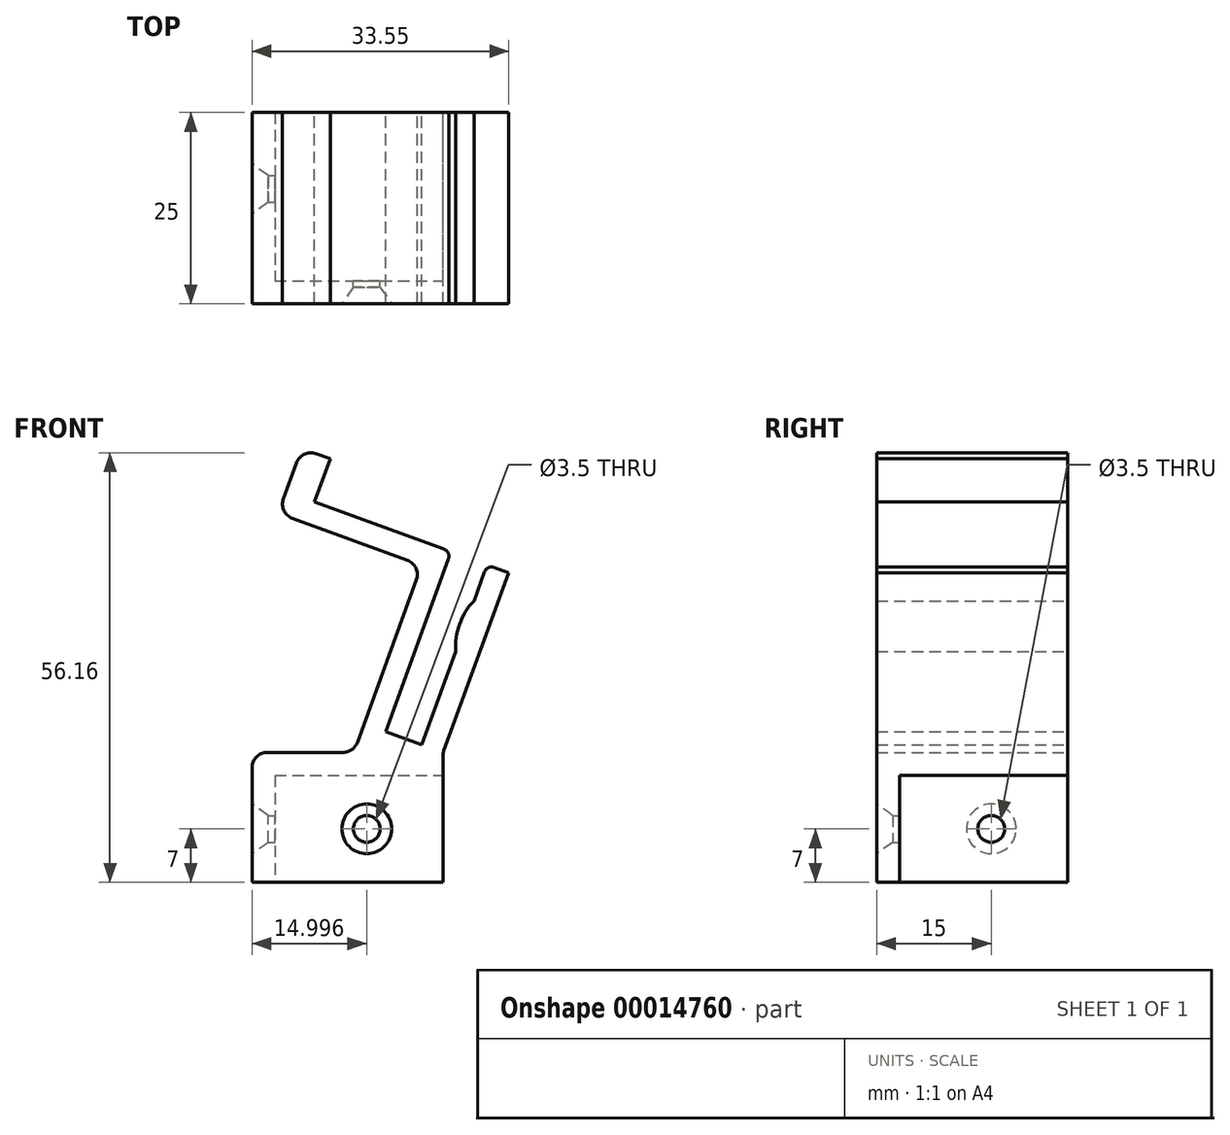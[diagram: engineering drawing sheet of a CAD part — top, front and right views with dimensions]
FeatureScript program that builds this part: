
annotation { "Feature Type Name" : "Feature", "Feature Type Description" : "" }
export const myFeature = defineFeature(function(context is Context, id is Id, definition is map)
    precondition{}
    {
        {
            var Q0;
            Q0=qCreatedBy(makeId("Front.planeOp"),FACE);
            var sketch = newSketch(context, id + "F0", { "sketchPlane" : qUnion([Q0])});
            skLineSegment(sketch, "E0", {"start": v(-18.57, 0) * mm, "end": v(-18.57, 1) * mm});
            skLineSegment(sketch, "E1", {"start": v(-10.2, 42.04) * mm, "end": v(-8.34, 41.37) * mm});
            skLineSegment(sketch, "E2", {"start": v(-8.34, 41.37) * mm, "end": v(-10.4, 35.73) * mm});
            skLineSegment(sketch, "E3", {"start": v(-10.4, 35.73) * mm, "end": v(6.52, 29.57) * mm});
            skLineSegment(sketch, "E4", {"start": v(7.12, 28.29) * mm, "end": v(-1.1, 5.74) * mm});
            skLineSegment(sketch, "E5", {"start": v(-1.1, 5.74) * mm, "end": v(3.6, 4.03) * mm});
            skLineSegment(sketch, "E6", {"start": v(3.6, 4.03) * mm, "end": v(8.04, 16.2) * mm});
            skArc(sketch, "E7", {"start": v(10.45, 22.82) * mm, "mid": v(8.56, 19.76) * mm, "end": v(8.04, 16.2) * mm});
            skLineSegment(sketch, "E8", {"start": v(10.45, 22.82) * mm, "end": v(11.82, 26.58) * mm});
            skLineSegment(sketch, "E9", {"start": v(13.1, 27.18) * mm, "end": v(14.98, 26.5) * mm});
            skLineSegment(sketch, "E10", {"start": v(14.98, 26.5) * mm, "end": v(6.49, 3.17) * mm});
            skLineSegment(sketch, "E11", {"start": v(6.43, 2.82) * mm, "end": v(6.43, 0) * mm});
            skLineSegment(sketch, "E12", {"start": v(6.43, 0) * mm, "end": v(-18.57, 0) * mm});
            skLineSegment(sketch, "E13", {"start": v(7.46, 29.23) * mm, "end": v(11.02, 27.93) * mm, "construction": true});
            skLineSegment(sketch, "E14", {"start": v(3.6, 4.03) * mm, "end": v(9.61, 1.84) * mm, "construction": true});
            skLineSegment(sketch, "E15", {"start": v(-12.76, 40.85) * mm, "end": v(-14.47, 36.15) * mm});
            skPoint(sketch, "E15.endSnap0", {"position": v(-18.57, 19.9) * mm});
            skPoint(sketch, "E16.orphan", {"position": v(-18.57, 39.81) * mm});
            skLineSegment(sketch, "E17", {"start": v(-18.57, 0) * mm, "end": v(-18.57, -14) * mm});
            skLineSegment(sketch, "E18", {"start": v(-18.57, -14) * mm, "end": v(6.43, -14) * mm});
            skLineSegment(sketch, "E19", {"start": v(6.43, -14) * mm, "end": v(6.43, 0) * mm});
            skPoint(sketch, "E20.visualSharp", {"position": v(-18.57, 24.88) * mm});
            skPoint(sketch, "E21.visualSharp", {"position": v(-12.08, 42.73) * mm});
            skArc(sketch, "E21.filletArc", {"start": v(-10.2, 42.04) * mm, "mid": v(-11.73, 41.97) * mm, "end": v(-12.76, 40.85) * mm});
            skPoint(sketch, "E22.visualSharp", {"position": v(12.16, 27.52) * mm});
            skArc(sketch, "E22.filletArc", {"start": v(13.1, 27.18) * mm, "mid": v(12.33, 27.14) * mm, "end": v(11.82, 26.58) * mm});
            skPoint(sketch, "E23.visualSharp", {"position": v(7.46, 29.23) * mm});
            skArc(sketch, "E23.filletArc", {"start": v(7.12, 28.29) * mm, "mid": v(7.08, 29.05) * mm, "end": v(6.52, 29.57) * mm});
            skPoint(sketch, "E24.visualSharp", {"position": v(6.43, 3) * mm});
            skArc(sketch, "E24.filletArc", {"start": v(6.49, 3.17) * mm, "mid": v(6.44, 3) * mm, "end": v(6.43, 2.82) * mm});
            skLineSegment(sketch, "E25", {"start": v(-9.68, 32.27) * mm, "end": v(1.73, 28.12) * mm});
            skLineSegment(sketch, "E26", {"start": v(2.93, 25.56) * mm, "end": v(-4.8, 4.32) * mm});
            skLineSegment(sketch, "E27", {"start": v(-9.68, 32.27) * mm, "end": v(-13.28, 33.58) * mm});
            skLineSegment(sketch, "E28", {"start": v(-6.68, 3) * mm, "end": v(-16.57, 3) * mm});
            skPoint(sketch, "E29.orphan", {"position": v(-4.8, 3) * mm});
            skPoint(sketch, "E30.visualSharp", {"position": v(-15.16, 34.27) * mm});
            skArc(sketch, "E30.filletArc", {"start": v(-14.47, 36.15) * mm, "mid": v(-14.4, 34.62) * mm, "end": v(-13.28, 33.58) * mm});
            skPoint(sketch, "E31.visualSharp", {"position": v(-18.57, 3) * mm});
            skArc(sketch, "E31.filletArc", {"start": v(-16.57, 3) * mm, "mid": v(-17.99, 2.41) * mm, "end": v(-18.57, 1) * mm});
            skPoint(sketch, "E32.visualSharp", {"position": v(3.61, 27.44) * mm});
            skArc(sketch, "E32.filletArc", {"start": v(2.93, 25.56) * mm, "mid": v(2.86, 27.09) * mm, "end": v(1.73, 28.12) * mm});
            skPoint(sketch, "E33.visualSharp", {"position": v(-5.28, 3) * mm});
            skArc(sketch, "E33.filletArc", {"start": v(-6.68, 3) * mm, "mid": v(-5.53, 3.36) * mm, "end": v(-4.8, 4.32) * mm});
            skSolve(sketch);
        }
        {
            var Q0;
            Q0=makeQuery(id+"F0.imprint","IMPRINT",FACE,{"disambiguationData":[TD([[makeQuery(id+"F0.imprint","IMPRINT",EDGE,{"derivedFrom":sQuery(id+"F0.wireOp",EDGE,"E0")}),-1.0]])]});
            var Q1;
            Q1=makeQuery(id+"F0.imprint","IMPRINT",FACE,{"disambiguationData":[TD([[makeQuery(id+"F0.imprint","IMPRINT",EDGE,{"derivedFrom":sQuery(id+"F0.wireOp",EDGE,"E12")}),1.0]])]});
            extrude(context, id + "F1", {"entities" : qUnion([Q0, Q1]), "depth" : 25 * mm});
        }
        {
            var Q0;
            Q0=makeQuery(id+"F1.opExtrude","SWEPT_FACE",FACE,{"disambiguationData":[OSD([sQuery(id+"F0.wireOp",EDGE,"E18")])]});
            var sketch = newSketch(context, id + "F2", { "sketchPlane" : qUnion([Q0])});
            skLineSegment(sketch, "E34.bottom", {"start": v(-15.57, 0) * mm, "end": v(6.43, 0) * mm});
            skLineSegment(sketch, "E34.top", {"start": v(-15.57, 22) * mm, "end": v(6.43, 22) * mm});
            skLineSegment(sketch, "E34.left", {"start": v(-15.57, 0) * mm, "end": v(-15.57, 22) * mm});
            skLineSegment(sketch, "E34.right", {"start": v(6.43, 0) * mm, "end": v(6.43, 22) * mm});
            skSolve(sketch);
        }
        {
            var Q0;
            Q0=makeQuery(id+"F2.imprint","IMPRINT",FACE,{"disambiguationData":[TD([[makeQuery(id+"F2.imprint","IMPRINT",EDGE,{"derivedFrom":sQuery(id+"F2.wireOp",EDGE,"E34.bottom")}),1.0]])]});
            extrude(context, id + "F3", {"entities" : qUnion([Q0]), "operationType" : NewBodyOperationType.REMOVE, "oppositeDirection" : true, "depth" : 14 * mm});
        }
        {
            var Q0;
            Q0=makeQuery(id+"F1.opExtrude","CAP_FACE",FACE,{"disambiguationData":[OSD([sQuery(id+"F0.wireOp",EDGE,"E0"),sQuery(id+"F0.wireOp",EDGE,"E1"),sQuery(id+"F0.wireOp",EDGE,"E2"),sQuery(id+"F0.wireOp",EDGE,"E3"),sQuery(id+"F0.wireOp",EDGE,"E4"),sQuery(id+"F0.wireOp",EDGE,"E5"),sQuery(id+"F0.wireOp",EDGE,"E6"),sQuery(id+"F0.wireOp",EDGE,"E7"),sQuery(id+"F0.wireOp",EDGE,"E8"),sQuery(id+"F0.wireOp",EDGE,"E9"),sQuery(id+"F0.wireOp",EDGE,"E10"),sQuery(id+"F0.wireOp",EDGE,"E11"),sQuery(id+"F0.wireOp",EDGE,"E15"),sQuery(id+"F0.wireOp",EDGE,"E17"),sQuery(id+"F0.wireOp",EDGE,"E18"),sQuery(id+"F0.wireOp",EDGE,"E19"),sQuery(id+"F0.wireOp",EDGE,"E20.filletArc"),sQuery(id+"F0.wireOp",EDGE,"E21.filletArc"),sQuery(id+"F0.wireOp",EDGE,"E22.filletArc"),sQuery(id+"F0.wireOp",EDGE,"E23.filletArc"),sQuery(id+"F0.wireOp",EDGE,"E24.filletArc")])],"isStart":false});
            var sketch = newSketch(context, id + "F4", { "sketchPlane" : qUnion([Q0])});
            skPoint(sketch, "E35", {"position": v(-3.57, -7) * mm});
            skSolve(sketch);
        }
        {
            var Q0;
            Q0=makeQuery(id+"F1.opExtrude","SWEPT_FACE",FACE,{"disambiguationData":[OSD([sQuery(id+"F0.wireOp",EDGE,"E0"),sQuery(id+"F0.wireOp",EDGE,"E17")])]});
            var sketch = newSketch(context, id + "F5", { "sketchPlane" : qUnion([Q0])});
            skPoint(sketch, "E36", {"position": v(10, -7) * mm});
            skSolve(sketch);
        }
        {
            var Q0;
            Q0=sQuery(id+"F5.wireOp",VERTEX,"E36");
            var Q1;
            Q1=makeQuery(id+"F1.opExtrude","SWEPT_BODY",BODY,{"disambiguationData":[OSD([sQuery(id+"F0.wireOp",EDGE,"E0"),sQuery(id+"F0.wireOp",EDGE,"E1"),sQuery(id+"F0.wireOp",EDGE,"E2"),sQuery(id+"F0.wireOp",EDGE,"E3"),sQuery(id+"F0.wireOp",EDGE,"E4"),sQuery(id+"F0.wireOp",EDGE,"E5"),sQuery(id+"F0.wireOp",EDGE,"E6"),sQuery(id+"F0.wireOp",EDGE,"E7"),sQuery(id+"F0.wireOp",EDGE,"E8"),sQuery(id+"F0.wireOp",EDGE,"E9"),sQuery(id+"F0.wireOp",EDGE,"E10"),sQuery(id+"F0.wireOp",EDGE,"E11"),sQuery(id+"F0.wireOp",EDGE,"E15"),sQuery(id+"F0.wireOp",EDGE,"E17"),sQuery(id+"F0.wireOp",EDGE,"E18"),sQuery(id+"F0.wireOp",EDGE,"E19"),sQuery(id+"F0.wireOp",EDGE,"E20.filletArc"),sQuery(id+"F0.wireOp",EDGE,"E21.filletArc"),sQuery(id+"F0.wireOp",EDGE,"E22.filletArc"),sQuery(id+"F0.wireOp",EDGE,"E23.filletArc"),sQuery(id+"F0.wireOp",EDGE,"E24.filletArc")])]});
            hole(context, id + "F6", {"style" : HoleStyle.C_SINK, "endStyle" : HoleEndStyle.BLIND, "holeDiameter" : 3.5 * mm, "cSinkDiameter" : 6.5 * mm, "cSinkAngle" : 70 * degree, "holeDepth" : 6 * mm, "locations" : qUnion([Q0]), "scope" : qUnion([Q1]), "startStyle" : HoleStartStyle.SKETCH});
        }
        {
            var Q0;
            Q0=sQuery(id+"F4.wireOp",VERTEX,"E35");
            var Q1;
            Q1=makeQuery(id+"F1.opExtrude","SWEPT_BODY",BODY,{"disambiguationData":[OSD([sQuery(id+"F0.wireOp",EDGE,"E0"),sQuery(id+"F0.wireOp",EDGE,"E1"),sQuery(id+"F0.wireOp",EDGE,"E2"),sQuery(id+"F0.wireOp",EDGE,"E3"),sQuery(id+"F0.wireOp",EDGE,"E4"),sQuery(id+"F0.wireOp",EDGE,"E5"),sQuery(id+"F0.wireOp",EDGE,"E6"),sQuery(id+"F0.wireOp",EDGE,"E7"),sQuery(id+"F0.wireOp",EDGE,"E8"),sQuery(id+"F0.wireOp",EDGE,"E9"),sQuery(id+"F0.wireOp",EDGE,"E10"),sQuery(id+"F0.wireOp",EDGE,"E11"),sQuery(id+"F0.wireOp",EDGE,"E15"),sQuery(id+"F0.wireOp",EDGE,"E17"),sQuery(id+"F0.wireOp",EDGE,"E18"),sQuery(id+"F0.wireOp",EDGE,"E19"),sQuery(id+"F0.wireOp",EDGE,"E20.filletArc"),sQuery(id+"F0.wireOp",EDGE,"E21.filletArc"),sQuery(id+"F0.wireOp",EDGE,"E22.filletArc"),sQuery(id+"F0.wireOp",EDGE,"E23.filletArc"),sQuery(id+"F0.wireOp",EDGE,"E24.filletArc")])]});
            hole(context, id + "F7", {"style" : HoleStyle.C_SINK, "endStyle" : HoleEndStyle.BLIND, "holeDiameter" : 3.5 * mm, "cSinkDiameter" : 6.5 * mm, "cSinkAngle" : 70 * degree, "holeDepth" : 6 * mm, "locations" : qUnion([Q0]), "scope" : qUnion([Q1]), "startStyle" : HoleStartStyle.SKETCH});
        }
    });
